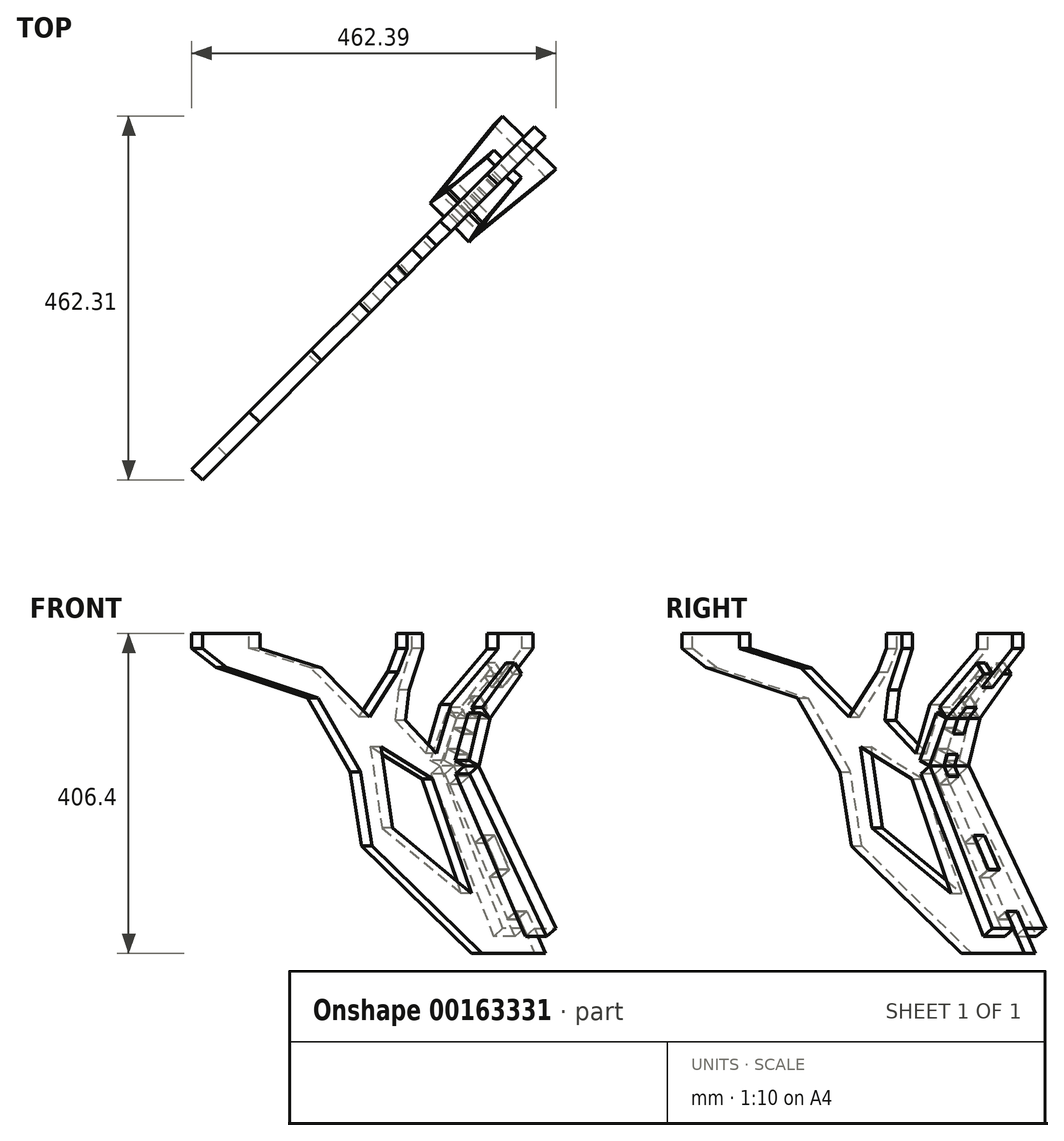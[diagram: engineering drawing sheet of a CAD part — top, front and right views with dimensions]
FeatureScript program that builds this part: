
annotation { "Feature Type Name" : "Feature", "Feature Type Description" : "" }
export const myFeature = defineFeature(function(context is Context, id is Id, definition is map)
    precondition{}
    {
        {
            var Q0;
            Q0=qCreatedBy(makeId("Top.planeOp"),FACE);
            var sketch = newSketch(context, id + "F0", { "sketchPlane" : qUnion([Q0])});
            skLineSegment(sketch, "E0.bottom", {"start": v(0, 1117.6) * mm, "end": v(558.8, 1117.6) * mm});
            skLineSegment(sketch, "E0.top", {"start": v(0, 0) * mm, "end": v(558.8, 0) * mm});
            skLineSegment(sketch, "E0.left", {"start": v(0, 1117.6) * mm, "end": v(0, 0) * mm});
            skLineSegment(sketch, "E0.right", {"start": v(558.8, 1117.6) * mm, "end": v(558.8, 0) * mm});
            skLineSegment(sketch, "E1", {"start": v(0, 0) * mm, "end": v(425.13, 425.13) * mm});
            skLineSegment(sketch, "E2", {"start": v(558.8, 0) * mm, "end": v(139.7, 419.1) * mm});
            skLineSegment(sketch, "E3", {"start": v(0, 1117.6) * mm, "end": v(428.86, 688.74) * mm});
            skLineSegment(sketch, "E4", {"start": v(558.8, 1117.6) * mm, "end": v(139.7, 698.5) * mm});
            skLineSegment(sketch, "E5", {"start": v(0, 1117.6) * mm, "end": v(139.7, 1117.6) * mm});
            skLineSegment(sketch, "E6", {"start": v(139.7, 1117.6) * mm, "end": v(139.7, -19.12) * mm});
            skLineSegment(sketch, "E7", {"start": v(558.8, 0) * mm, "end": v(419.1, 0) * mm});
            skLineSegment(sketch, "E8", {"start": v(419.1, 0) * mm, "end": v(434.94, 1117.6) * mm});
            skSolve(sketch);
        }
        {
            var Q0;
            Q0=sQuery(id+"F0.wireOp",EDGE,"E4");
            var Q1;
            {var subQ0=sQuery(id+"F0.wireOp",EDGE,"E6");var subQ1=sQuery(id+"F0.wireOp",EDGE,"E3");var subQ2=makeQuery(id+"F0.imprint","INTERSECT",VERTEX,{"derivedFrom":[subQ1,subQ0]});Q1=makeQuery(id+"F0.imprint","IMPRINT",FACE,{"disambiguationData":[TD([[makeQuery(id+"F0.imprint","IMPRINT",EDGE,{"disambiguationData":[TD([[subQ2,-1.0]])],"derivedFrom":subQ1}),-1.0]])]});}
            cPlane(context, id + "F1", {"entities" : qUnion([Q0, Q1]), "cplaneType" : CPlaneType.LINE_ANGLE, "offset" : 25.4 * mm, "angle" : 90 * degree, "width" : 152.4 * mm, "height" : 152.4 * mm});
        }
        {
            var Q0;
            Q0=sQuery(id+"F0.wireOp",EDGE,"E3");
            cPlane(context, id + "F2", {"entities" : qUnion([Q0]), "cplaneType" : CPlaneType.LINE_ANGLE, "offset" : 25.4 * mm, "angle" : 90 * degree, "width" : 152.4 * mm, "height" : 152.4 * mm});
        }
        {
            var Q0;
            Q0=qCreatedBy(id+"F1.planeOp",FACE);
            var sketch = newSketch(context, id + "F3", { "sketchPlane" : qUnion([Q0])});
            skLineSegment(sketch, "E9", {"start": v(1094.94, 0) * mm, "end": v(897.34, 136.4) * mm});
            skLineSegment(sketch, "E10", {"start": v(897.34, 136.4) * mm, "end": v(876.9, 230.57) * mm});
            skLineSegment(sketch, "E11", {"start": v(636.42, 363.23) * mm, "end": v(592.7, 387.35) * mm});
            skLineSegment(sketch, "E12", {"start": v(892.75, 300.26) * mm, "end": v(944.32, 357.83) * mm});
            skLineSegment(sketch, "E13", {"start": v(913.31, 262.32) * mm, "end": v(934.51, 159.58) * mm});
            skLineSegment(sketch, "E14", {"start": v(934.51, 159.58) * mm, "end": v(1076.6, 76.51) * mm});
            skLineSegment(sketch, "E15", {"start": v(1076.6, 76.51) * mm, "end": v(1005.95, 221.4) * mm});
            skLineSegment(sketch, "E16", {"start": v(1005.95, 221.4) * mm, "end": v(913.31, 262.32) * mm});
            skLineSegment(sketch, "E17", {"start": v(1094.94, 0) * mm, "end": v(1186.35, 0) * mm});
            skLineSegment(sketch, "E18", {"start": v(964.34, 334.44) * mm, "end": v(957.99, 295.95) * mm});
            skLineSegment(sketch, "E19", {"start": v(957.99, 295.95) * mm, "end": v(1013.51, 254.38) * mm});
            skLineSegment(sketch, "E20", {"start": v(1013.51, 254.38) * mm, "end": v(1038.93, 316.2) * mm});
            skLineSegment(sketch, "E21", {"start": v(1038.93, 316.2) * mm, "end": v(1123.42, 386.95) * mm});
            skLineSegment(sketch, "E22", {"start": v(892.75, 300.26) * mm, "end": v(807.06, 362.34) * mm});
            skLineSegment(sketch, "E23", {"start": v(807.06, 362.34) * mm, "end": v(696.04, 387.35) * mm});
            skLineSegment(sketch, "E24", {"start": v(636.42, 363.23) * mm, "end": v(800.62, 324.38) * mm});
            skLineSegment(sketch, "E25", {"start": v(800.62, 324.38) * mm, "end": v(876.9, 230.57) * mm});
            skLineSegment(sketch, "E26", {"start": v(964.34, 334.44) * mm, "end": v(988.36, 387.35) * mm});
            skLineSegment(sketch, "E27", {"start": v(592.7, 406.4) * mm, "end": v(1186.35, 406.4) * mm, "construction": true});
            skLineSegment(sketch, "E28", {"start": v(996.91, 406.4) * mm, "end": v(996.91, 387.35) * mm});
            skLineSegment(sketch, "E29", {"start": v(1186.35, 387.35) * mm, "end": v(592.7, 387.35) * mm, "construction": true});
            skLineSegment(sketch, "E30.0", {"start": v(1088.6, 298.37) * mm, "end": v(1186.35, 387.24) * mm, "construction": true});
            skLineSegment(sketch, "E31.0", {"start": v(1063.72, 238.1) * mm, "end": v(1088.6, 298.37) * mm, "construction": true});
            skLineSegment(sketch, "E32", {"start": v(1137.96, 368.99) * mm, "end": v(1150.78, 354.9) * mm, "construction": true});
            skLineSegment(sketch, "E33", {"start": v(1150.78, 354.9) * mm, "end": v(1186.35, 387.35) * mm});
            skLineSegment(sketch, "E34", {"start": v(1186.35, 387.35) * mm, "end": v(1186.35, 406.4) * mm});
            skLineSegment(sketch, "E35", {"start": v(1123.42, 386.95) * mm, "end": v(1123.42, 406.4) * mm});
            skLineSegment(sketch, "E36", {"start": v(1123.42, 406.4) * mm, "end": v(1186.35, 406.4) * mm});
            skLineSegment(sketch, "E37", {"start": v(988.36, 387.35) * mm, "end": v(988.36, 406.4) * mm});
            skLineSegment(sketch, "E38", {"start": v(944.32, 357.83) * mm, "end": v(960.38, 387.35) * mm});
            skLineSegment(sketch, "E39", {"start": v(960.38, 387.35) * mm, "end": v(960.38, 406.4) * mm});
            skLineSegment(sketch, "E40", {"start": v(960.38, 406.4) * mm, "end": v(988.36, 406.4) * mm});
            skLineSegment(sketch, "E41", {"start": v(696.04, 387.35) * mm, "end": v(696.04, 406.4) * mm});
            skLineSegment(sketch, "E42", {"start": v(592.7, 387.35) * mm, "end": v(592.7, 406.4) * mm});
            skLineSegment(sketch, "E43", {"start": v(696.04, 406.4) * mm, "end": v(592.7, 406.4) * mm});
            skLineSegment(sketch, "E44", {"start": v(1042.43, 236.43) * mm, "end": v(1052.15, 259.98) * mm, "construction": true});
            skLineSegment(sketch, "E45", {"start": v(1052.15, 259.98) * mm, "end": v(1069.76, 252.71) * mm});
            skLineSegment(sketch, "E46", {"start": v(1069.76, 252.71) * mm, "end": v(1063.72, 238.1) * mm});
            skLineSegment(sketch, "E47", {"start": v(1042.43, 236.43) * mm, "end": v(1055.63, 214.75) * mm, "construction": true});
            skLineSegment(sketch, "E48", {"start": v(1055.63, 214.75) * mm, "end": v(1071.9, 224.65) * mm});
            skLineSegment(sketch, "E49", {"start": v(1071.9, 224.65) * mm, "end": v(1063.72, 238.1) * mm});
            skLineSegment(sketch, "E50", {"start": v(1062.96, 286.17) * mm, "end": v(1080.57, 278.9) * mm});
            skLineSegment(sketch, "E51", {"start": v(1080.57, 278.9) * mm, "end": v(1088.6, 298.37) * mm});
            skLineSegment(sketch, "E52", {"start": v(1072.63, 309.59) * mm, "end": v(1091.4, 326.66) * mm, "construction": true});
            skLineSegment(sketch, "E53", {"start": v(1091.4, 326.66) * mm, "end": v(1104.23, 312.57) * mm});
            skLineSegment(sketch, "E54", {"start": v(1104.23, 312.57) * mm, "end": v(1088.6, 298.37) * mm});
            skLineSegment(sketch, "E55", {"start": v(1150.78, 354.9) * mm, "end": v(1131.94, 337.77) * mm});
            skLineSegment(sketch, "E56", {"start": v(1131.94, 337.77) * mm, "end": v(1119.12, 351.86) * mm});
            skLineSegment(sketch, "E57", {"start": v(1186.35, 0) * mm, "end": v(1173.09, 21.78) * mm, "construction": true});
            skLineSegment(sketch, "E58", {"start": v(1173.09, 21.78) * mm, "end": v(1189.36, 31.69) * mm, "construction": true});
            skLineSegment(sketch, "E59", {"start": v(1189.36, 31.69) * mm, "end": v(1208.65, 0) * mm});
            skLineSegment(sketch, "E60", {"start": v(1208.65, 0) * mm, "end": v(1186.35, 0) * mm});
            skPoint(sketch, "E61", {"position": v(1130.63, 128.17) * mm});
            skLineSegment(sketch, "E62", {"start": v(1130.63, 128.17) * mm, "end": v(1114.39, 118.22) * mm, "construction": true});
            skLineSegment(sketch, "E63", {"start": v(1114.39, 118.22) * mm, "end": v(1101.18, 139.92) * mm, "construction": true});
            skLineSegment(sketch, "E64", {"start": v(1101.18, 139.92) * mm, "end": v(1117.45, 149.82) * mm});
            skLineSegment(sketch, "E65", {"start": v(1114.39, 118.22) * mm, "end": v(1127.6, 96.52) * mm, "construction": true});
            skLineSegment(sketch, "E66", {"start": v(1127.6, 96.52) * mm, "end": v(1143.86, 106.43) * mm});
            skLineSegment(sketch, "E67", {"start": v(1143.86, 106.43) * mm, "end": v(1117.45, 149.82) * mm});
            skLineSegment(sketch, "E68", {"start": v(1055.63, 214.75) * mm, "end": v(1101.18, 139.92) * mm});
            skLineSegment(sketch, "E69", {"start": v(1127.6, 96.52) * mm, "end": v(1159.9, 43.45) * mm});
            skLineSegment(sketch, "E70", {"start": v(1137.96, 368.99) * mm, "end": v(1119.12, 351.86) * mm, "construction": true});
            skLineSegment(sketch, "E71", {"start": v(1091.4, 326.66) * mm, "end": v(1119.12, 351.86) * mm});
            skLineSegment(sketch, "E72", {"start": v(1072.63, 309.59) * mm, "end": v(1062.96, 286.17) * mm, "construction": true});
            skLineSegment(sketch, "E73", {"start": v(1052.15, 259.98) * mm, "end": v(1062.96, 286.17) * mm});
            skLineSegment(sketch, "E74", {"start": v(1189.36, 31.69) * mm, "end": v(1176.17, 53.36) * mm});
            skLineSegment(sketch, "E75", {"start": v(1176.17, 53.36) * mm, "end": v(1159.9, 43.45) * mm});
            skSolve(sketch);
        }
        {
            var Q0;
            Q0=makeQuery(id+"F3.imprint","IMPRINT",FACE,{"disambiguationData":[TD([[makeQuery(id+"F3.imprint","IMPRINT",EDGE,{"derivedFrom":sQuery(id+"F3.wireOp",EDGE,"E9")}),-1.0]])]});
            extrude(context, id + "F4", {"entities" : qUnion([Q0]), "endBound" : BoundingType.SYMMETRIC, "depth" : 19.05 * mm});
        }
        {
            var Q0;
            Q0=makeQuery(id+"F4.opExtrude","SWEPT_FACE",FACE,{"disambiguationData":[OSD([sQuery(id+"F3.wireOp",EDGE,"E69")])]});
            cPlane(context, id + "F5", {"entities" : qUnion([Q0]), "cplaneType" : CPlaneType.OFFSET, "offset" : 0 * mm, "width" : 152.4 * mm, "height" : 152.4 * mm});
        }
        {
            var Q0;
            Q0=qCreatedBy(id+"F5.planeOp",FACE);
            var sketch = newSketch(context, id + "F6", { "sketchPlane" : qUnion([Q0])});
            skLineSegment(sketch, "E76", {"start": v(180.73, -488.17) * mm, "end": v(173.47, -502.13) * mm});
            skLineSegment(sketch, "E77", {"start": v(150.08, -588.62) * mm, "end": v(126.6, -633.81) * mm});
            skLineSegment(sketch, "E78", {"start": v(109.61, -624.99) * mm, "end": v(126.6, -633.81) * mm});
            skLineSegment(sketch, "E79", {"start": v(98, -688.84) * mm, "end": v(81.02, -680) * mm});
            skLineSegment(sketch, "E80", {"start": v(133.1, -579.8) * mm, "end": v(150.08, -588.62) * mm});
            skLineSegment(sketch, "E81", {"start": v(173.47, -502.13) * mm, "end": v(190.45, -510.96) * mm});
            skLineSegment(sketch, "E82", {"start": v(190.45, -510.96) * mm, "end": v(197.7, -497) * mm});
            skLineSegment(sketch, "E83", {"start": v(81.02, -680) * mm, "end": v(69.3, -702.55) * mm});
            skLineSegment(sketch, "E84", {"start": v(69.3, -702.55) * mm, "end": v(86.2, -711.34) * mm});
            skLineSegment(sketch, "E85", {"start": v(86.2, -711.34) * mm, "end": v(98, -688.84) * mm});
            skLineSegment(sketch, "E86", {"start": v(86.2, -711.34) * mm, "end": v(120, -728.91) * mm});
            skLineSegment(sketch, "E87", {"start": v(69.3, -702.55) * mm, "end": v(35.43, -684.95) * mm});
            skLineSegment(sketch, "E88", {"start": v(197.7, -497) * mm, "end": v(220.23, -508.7) * mm});
            skLineSegment(sketch, "E89", {"start": v(180.8, -488.21) * mm, "end": v(158.23, -476.48) * mm});
            skLineSegment(sketch, "E90", {"start": v(158.23, -476.48) * mm, "end": v(35.43, -684.95) * mm});
            skLineSegment(sketch, "E91", {"start": v(220.23, -508.7) * mm, "end": v(120, -728.91) * mm});
            skLineSegment(sketch, "E92.trimOffspring", {"start": v(133.1, -579.8) * mm, "end": v(109.61, -624.99) * mm});
            skSolve(sketch);
        }
        {
            var Q0;
            {var subQ0=sQuery(id+"F6.wireOp",EDGE,"E76");Q0=makeQuery(id+"F6.imprint","IMPRINT",FACE,{"disambiguationData":[TD([[makeQuery(id+"F6.imprint","IMPRINT",EDGE,{"derivedFrom":subQ0}),-1.0]])]});}
            extrude(context, id + "F7", {"entities" : qUnion([Q0]), "depth" : 19.05 * mm});
        }
        {
            var Q0;
            Q0=makeQuery(id+"F4.opExtrude","SWEPT_FACE",FACE,{"disambiguationData":[OSD([sQuery(id+"F3.wireOp",EDGE,"E73")])]});
            cPlane(context, id + "F8", {"entities" : qUnion([Q0]), "cplaneType" : CPlaneType.OFFSET, "offset" : 0 * mm, "width" : 152.4 * mm, "height" : 152.4 * mm});
        }
        {
            var Q0;
            Q0=qCreatedBy(id+"F8.planeOp",FACE);
            var sketch = newSketch(context, id + "F9", { "sketchPlane" : qUnion([Q0])});
            skLineSegment(sketch, "E93", {"start": v(149.23, 743.92) * mm, "end": v(131.14, 737.01) * mm});
            skLineSegment(sketch, "E94", {"start": v(131.14, 737.01) * mm, "end": v(136.78, 722.23) * mm});
            skLineSegment(sketch, "E95", {"start": v(136.78, 722.23) * mm, "end": v(113.1, 713.19) * mm});
            skLineSegment(sketch, "E96", {"start": v(149.23, 743.92) * mm, "end": v(154.87, 729.14) * mm});
            skLineSegment(sketch, "E97", {"start": v(154.87, 729.14) * mm, "end": v(178.56, 738.18) * mm});
            skLineSegment(sketch, "E98", {"start": v(139.13, 770.38) * mm, "end": v(131.62, 790.06) * mm});
            skLineSegment(sketch, "E99", {"start": v(139.13, 770.38) * mm, "end": v(121.33, 763.59) * mm});
            skLineSegment(sketch, "E100", {"start": v(121.33, 763.59) * mm, "end": v(113.82, 783.27) * mm});
            skLineSegment(sketch, "E101", {"start": v(113.82, 783.27) * mm, "end": v(94.6, 775.93) * mm});
            skLineSegment(sketch, "E102", {"start": v(94.6, 775.93) * mm, "end": v(113.1, 713.19) * mm});
            skLineSegment(sketch, "E103", {"start": v(131.62, 790.06) * mm, "end": v(150.85, 797.4) * mm});
            skLineSegment(sketch, "E104", {"start": v(150.85, 797.4) * mm, "end": v(178.56, 738.18) * mm});
            skSolve(sketch);
        }
        {
            var Q0;
            Q0=makeQuery(id+"F9.imprint","IMPRINT",FACE,{"disambiguationData":[TD([[makeQuery(id+"F9.imprint","IMPRINT",EDGE,{"derivedFrom":sQuery(id+"F9.wireOp",EDGE,"E93")}),-1.0]])]});
            extrude(context, id + "F10", {"entities" : qUnion([Q0]), "depth" : 19.05 * mm});
        }
        {
            var Q0;
            Q0=makeQuery(id+"F4.opExtrude","SWEPT_FACE",FACE,{"disambiguationData":[OSD([sQuery(id+"F3.wireOp",EDGE,"E71")])]});
            cPlane(context, id + "F11", {"entities" : qUnion([Q0]), "cplaneType" : CPlaneType.OFFSET, "offset" : 0 * mm, "width" : 152.4 * mm, "height" : 152.4 * mm});
        }
        {
            var Q0;
            Q0=qCreatedBy(id+"F11.planeOp",FACE);
            var sketch = newSketch(context, id + "F12", { "sketchPlane" : qUnion([Q0])});
            skLineSegment(sketch, "E105", {"start": v(323.3, -1085.27) * mm, "end": v(307.98, -1096.6) * mm});
            skLineSegment(sketch, "E106", {"start": v(307.98, -1096.6) * mm, "end": v(323.1, -1117.02) * mm});
            skLineSegment(sketch, "E107", {"start": v(323.1, -1117.02) * mm, "end": v(310.83, -1126.1) * mm});
            skLineSegment(sketch, "E108", {"start": v(323.3, -1085.27) * mm, "end": v(338.4, -1105.69) * mm});
            skLineSegment(sketch, "E109", {"start": v(338.4, -1105.69) * mm, "end": v(350.93, -1097) * mm});
            skLineSegment(sketch, "E110", {"start": v(301.02, -1055.16) * mm, "end": v(285.7, -1066.5) * mm});
            skLineSegment(sketch, "E111", {"start": v(285.7, -1066.5) * mm, "end": v(273.15, -1049.52) * mm});
            skLineSegment(sketch, "E112", {"start": v(301.02, -1055.16) * mm, "end": v(288.46, -1038.2) * mm});
            skLineSegment(sketch, "E113", {"start": v(273.15, -1049.52) * mm, "end": v(256.62, -1061.76) * mm});
            skLineSegment(sketch, "E114", {"start": v(256.62, -1061.76) * mm, "end": v(310.83, -1126.1) * mm});
            skLineSegment(sketch, "E115", {"start": v(288.46, -1038.2) * mm, "end": v(305, -1025.96) * mm});
            skLineSegment(sketch, "E116", {"start": v(305, -1025.96) * mm, "end": v(350.93, -1097) * mm});
            skSolve(sketch);
        }
        {
            var Q0;
            Q0=makeQuery(id+"F12.imprint","IMPRINT",FACE,{"disambiguationData":[TD([[makeQuery(id+"F12.imprint","IMPRINT",EDGE,{"derivedFrom":sQuery(id+"F12.wireOp",EDGE,"E105")}),-1.0]])]});
            extrude(context, id + "F13", {"entities" : qUnion([Q0]), "depth" : 19.05 * mm});
        }
    });
